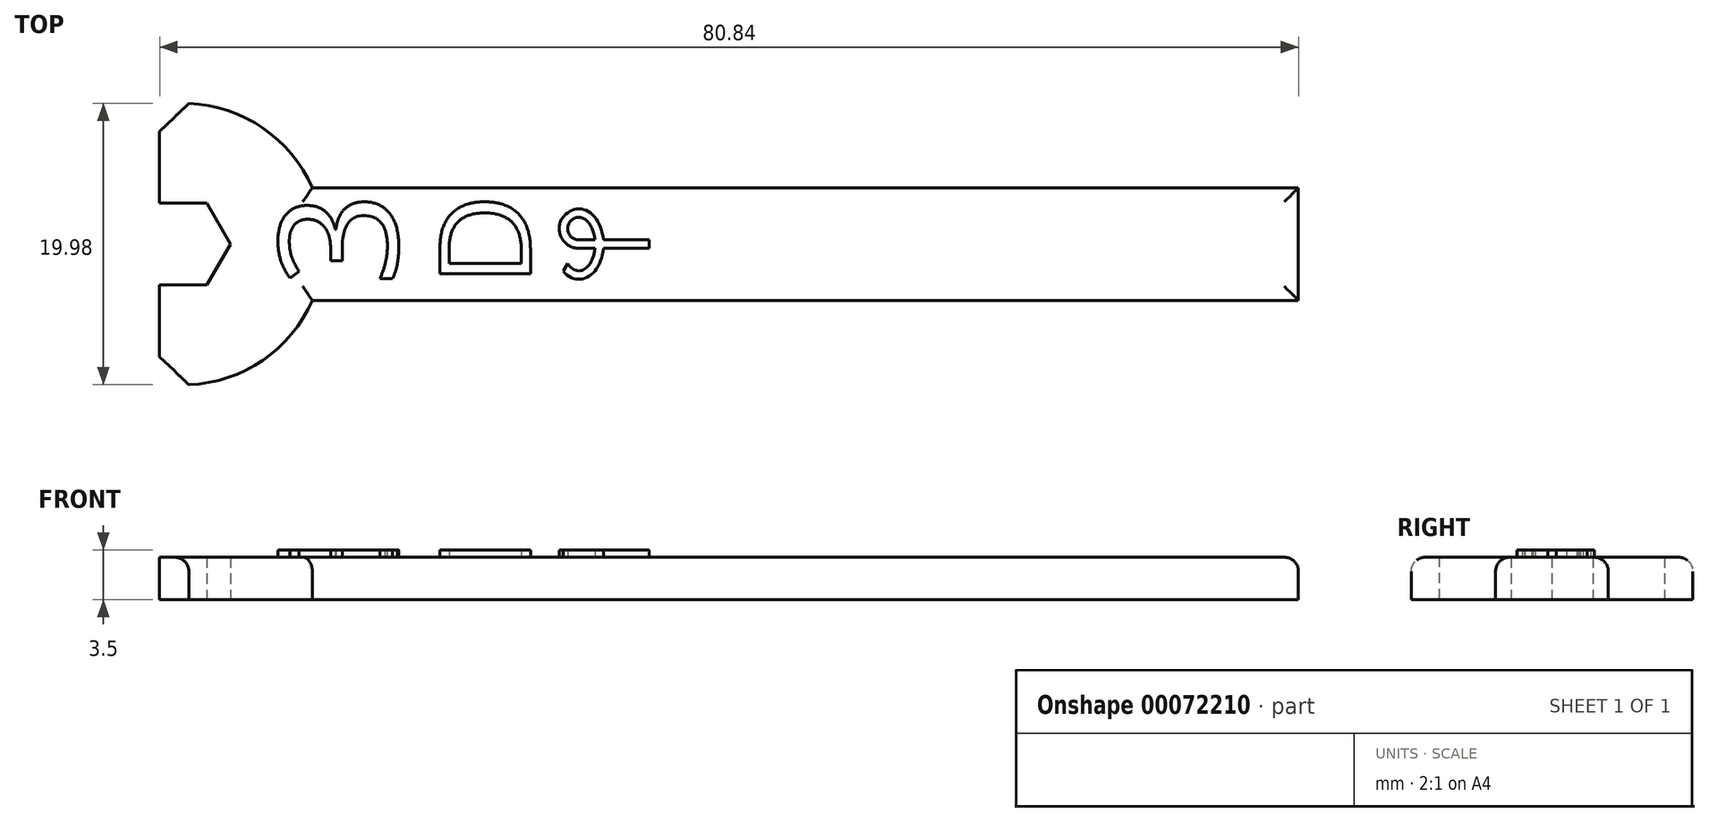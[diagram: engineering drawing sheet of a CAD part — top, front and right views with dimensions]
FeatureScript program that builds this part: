
annotation { "Feature Type Name" : "Feature", "Feature Type Description" : "" }
export const myFeature = defineFeature(function(context is Context, id is Id, definition is map)
    precondition{}
    {
        {
            var Q0;
            Q0=qCreatedBy(makeId("Top.planeOp"),FACE);
            var sketch = newSketch(context, id + "F0", { "sketchPlane" : qUnion([Q0])});
            skCircle(sketch, "E0.cCircle", {"center": v(0, 0) * mm, "radius": 2.9 * mm, "construction": true});
            skLineSegment(sketch, "E0.0", {"start": v(-3.35, 0) * mm, "end": v(-1.67, 2.9) * mm, "construction": true});
            skLineSegment(sketch, "E0.1", {"start": v(-1.67, 2.9) * mm, "end": v(1.67, 2.9) * mm});
            skLineSegment(sketch, "E0.2", {"start": v(1.67, 2.9) * mm, "end": v(3.35, 0) * mm});
            skLineSegment(sketch, "E0.3", {"start": v(3.35, 0) * mm, "end": v(1.67, -2.9) * mm});
            skLineSegment(sketch, "E0.4", {"start": v(1.67, -2.9) * mm, "end": v(-1.67, -2.9) * mm});
            skLineSegment(sketch, "E0.5", {"start": v(-1.67, -2.9) * mm, "end": v(-3.35, 0) * mm, "construction": true});
            skArc(sketch, "E1", {"start": v(9.17, 4) * mm, "mid": v(4.75, 8.8) * mm, "end": v(-1.67, 9.86) * mm});
            skLineSegment(sketch, "E2.bottom", {"start": v(9.17, 4) * mm, "end": v(79.17, 4) * mm});
            skLineSegment(sketch, "E2.top", {"start": v(9.17, -4) * mm, "end": v(79.17, -4) * mm});
            skLineSegment(sketch, "E2.right", {"start": v(79.17, 4) * mm, "end": v(79.17, -4) * mm});
            skArc(sketch, "E3.trimOffspring", {"start": v(-1.67, -9.86) * mm, "mid": v(4.75, -8.8) * mm, "end": v(9.17, -4) * mm});
            skLineSegment(sketch, "E4", {"start": v(-1.67, -9.86) * mm, "end": v(-1.67, -2.9) * mm});
            skLineSegment(sketch, "E5", {"start": v(-1.67, 2.9) * mm, "end": v(-1.67, 9.86) * mm});
            skSolve(sketch);
        }
        {
            var Q0;
            Q0=qSketchRegion(id+"F0",true);
            extrude(context, id + "F1", {"entities" : qUnion([Q0]), "depth" : 3 * mm});
        }
        {
            var Q0;
            Q0=makeQuery(id+"F1.opExtrude","SWEPT_EDGE",EDGE,{"disambiguationData":[OSD([sQuery(id+"F0.wireOp",EDGE,"E3.trimOffspring"),sQuery(id+"F0.wireOp",EDGE,"E4")])]});
            var Q1;
            Q1=makeQuery(id+"F1.opExtrude","SWEPT_EDGE",EDGE,{"disambiguationData":[OSD([sQuery(id+"F0.wireOp",EDGE,"E1"),sQuery(id+"F0.wireOp",EDGE,"E5")])]});
            chamfer(context, id + "F2", {"entities" : qUnion([Q0, Q1]), "width" : 2 * mm, "tangentPropagation" : true});
        }
        {
            var Q0;
            Q0=makeQuery(id+"F1.opExtrude","CAP_EDGE",EDGE,{"disambiguationData":[OSD([sQuery(id+"F0.wireOp",EDGE,"E1")])],"isStart":false});
            var Q1;
            Q1=makeQuery(id+"F1.opExtrude","CAP_EDGE",EDGE,{"disambiguationData":[OSD([sQuery(id+"F0.wireOp",EDGE,"E2.top")])],"isStart":false});
            var Q2;
            Q2=makeQuery(id+"F1.opExtrude","CAP_EDGE",EDGE,{"disambiguationData":[OSD([sQuery(id+"F0.wireOp",EDGE,"E2.bottom")])],"isStart":false});
            var Q3;
            Q3=makeQuery(id+"F1.opExtrude","CAP_EDGE",EDGE,{"disambiguationData":[OSD([sQuery(id+"F0.wireOp",EDGE,"E2.right")])],"isStart":false});
            var Q4;
            Q4=makeQuery(id+"F1.opExtrude","CAP_EDGE",EDGE,{"disambiguationData":[OSD([sQuery(id+"F0.wireOp",EDGE,"E3.trimOffspring")])],"isStart":false});
            fillet(context, id + "F3", {"entities" : qUnion([Q0, Q1, Q2, Q3, Q4]), "radius" : 1 * mm, "tangentPropagation" : true, "allowEdgeOverflow" : false});
        }
        {
            var Q0;
            Q0=makeQuery(id+"F1.opExtrude","CAP_FACE",FACE,{"disambiguationData":[OSD([sQuery(id+"F0.wireOp",EDGE,"E0.0"),sQuery(id+"F0.wireOp",EDGE,"E0.1"),sQuery(id+"F0.wireOp",EDGE,"E0.2"),sQuery(id+"F0.wireOp",EDGE,"E0.3"),sQuery(id+"F0.wireOp",EDGE,"E0.4"),sQuery(id+"F0.wireOp",EDGE,"E0.5"),sQuery(id+"F0.wireOp",EDGE,"E1"),sQuery(id+"F0.wireOp",EDGE,"E2.bottom"),sQuery(id+"F0.wireOp",EDGE,"E2.top"),sQuery(id+"F0.wireOp",EDGE,"E2.right")])],"isStart":false});
            var sketch = newSketch(context, id + "F4", { "sketchPlane" : qUnion([Q0])});
            skText(sketch, "E6", { "text": "3\n", "fontName": "OpenSans-Regular.ttf"});
            skText(sketch, "E7", { "text": "D", "fontName": "OpenSans-Regular.ttf"});
            const initialGuessF4  = {"E6": [0.01519, -0.003, 0, 1, 0.00842], "E7": [0.02465, -0.003, 0, 1, 0.00647]};
            skSetInitialGuess(sketch, initialGuessF4);
            skSolve(sketch);
        }
        {
            var Q0;
            Q0=qSketchRegion(id+"F4",true);
            extrude(context, id + "F5", {"entities" : qUnion([Q0]), "operationType" : NewBodyOperationType.ADD, "depth" : 0.5 * mm});
        }
        {
            var Q0;
            Q0=makeQuery(id+"F4.imprint","IMPRINT",FACE,{"disambiguationData":[TD([[makeQuery(id+"F4.imprint","IMPRINT",EDGE,{"derivedFrom":sQuery(id+"F4.wireOp",EDGE,"E6.sketch_text.stroke-0")}),1.0]])]});
            var sketch = newSketch(context, id + "F6", { "sketchPlane" : qUnion([Q0])});
            skLineSegment(sketch, "E8.rect.bottom", {"start": v(28.09, 0.3) * mm, "end": v(33.09, 0.3) * mm});
            skLineSegment(sketch, "E8.rect.top", {"start": v(28.09, -0.3) * mm, "end": v(33.09, -0.3) * mm});
            skLineSegment(sketch, "E8.rect.left", {"start": v(28.09, 0.3) * mm, "end": v(28.09, -0.3) * mm});
            skLineSegment(sketch, "E8.rect.right", {"start": v(33.09, 0.3) * mm, "end": v(33.09, -0.3) * mm});
            skPoint(sketch, "E8.rect.middle", {"position": v(30.59, 0) * mm});
            skLineSegment(sketch, "E9", {"start": v(28.09, 0.3) * mm, "end": v(28.09, 4.53) * mm, "construction": true});
            skArc(sketch, "E10", {"start": v(28.09, 1.9) * mm, "mid": v(27.29, 1.1) * mm, "end": v(28.09, 0.3) * mm});
            skArc(sketch, "E11", {"start": v(28.09, 2.5) * mm, "mid": v(26.69, 1.1) * mm, "end": v(28.09, -0.3) * mm});
            skPoint(sketch, "E12", {"position": v(28.09, 0) * mm});
            skEllipse(sketch, "E13", {"center": v(28.09, 0) * mm, "majorRadius": 2.5 * mm, "minorRadius": 1.75 * mm, "majorAxis": v(0, 1)});
            skEllipse(sketch, "E14", {"center": v(28.09, 0) * mm, "majorRadius": 1.9 * mm, "minorRadius": 1.15 * mm, "majorAxis": v(0, 1)});
            skLineSegment(sketch, "E15", {"start": v(28.09, 0) * mm, "end": v(26.98, -1.93) * mm});
            skPoint(sketch, "E16", {"position": v(27.3, -1.37) * mm});
            skPoint(sketch, "E17", {"position": v(26.98, -1.93) * mm});
            skSolve(sketch);
        }
        {
            var Q0;
            {var subQ0=sQuery(id+"F6.wireOp",EDGE,"E8.rect.right");Q0=makeQuery(id+"F6.imprint","IMPRINT",FACE,{"disambiguationData":[TD([[makeQuery(id+"F6.imprint","IMPRINT",EDGE,{"derivedFrom":subQ0}),-1.0]])]});}
            var Q1;
            {var subQ0=sQuery(id+"F6.wireOp",EDGE,"E14");var subQ1=sQuery(id+"F6.wireOp",EDGE,"E8.rect.bottom");var subQ2=makeQuery(id+"F6.imprint","INTERSECT",VERTEX,{"derivedFrom":[subQ1,subQ0]});Q1=makeQuery(id+"F6.imprint","IMPRINT",FACE,{"disambiguationData":[TD([[makeQuery(id+"F6.imprint","IMPRINT",EDGE,{"disambiguationData":[TD([[subQ2,-1.0]])],"derivedFrom":subQ1}),-1.0]])]});}
            var Q2;
            {var subQ4=sQuery(id+"F6.wireOp",EDGE,"E14");var subQ6=sQuery(id+"F6.wireOp",EDGE,"E8.rect.bottom");var subQ8=makeQuery(id+"F6.imprint","INTERSECT",VERTEX,{"derivedFrom":[subQ6,subQ4]});Q2=makeQuery(id+"F6.imprint","IMPRINT",FACE,{"disambiguationData":[TD([[makeQuery(id+"F6.imprint","IMPRINT",EDGE,{"disambiguationData":[TD([[subQ8,1.0]])],"derivedFrom":subQ4}),1.0]])]});}
            var Q3;
            {var subQ1=sQuery(id+"F6.wireOp",EDGE,"E8.rect.left");var subQ3=sQuery(id+"F6.wireOp",EDGE,"E15");var subQ4=makeQuery(id+"F6.imprint","INTERSECT",VERTEX,{"derivedFrom":[subQ1,subQ3]});Q3=makeQuery(id+"F6.imprint","IMPRINT",FACE,{"disambiguationData":[TD([[makeQuery(id+"F6.imprint","IMPRINT",EDGE,{"disambiguationData":[TD([[subQ4,-1.0]])],"derivedFrom":subQ3}),1.0]])]});}
            var Q4;
            {var subQ1=sQuery(id+"F6.wireOp",EDGE,"E10");Q4=makeQuery(id+"F6.imprint","IMPRINT",FACE,{"disambiguationData":[TD([[makeQuery(id+"F6.imprint","IMPRINT",EDGE,{"derivedFrom":subQ1}),-1.0]])]});}
            var Q5;
            {var subQ0=sQuery(id+"F6.wireOp",EDGE,"E14");var subQ6=sQuery(id+"F6.wireOp",EDGE,"E8.rect.bottom");var subQ8=makeQuery(id+"F6.imprint","INTERSECT",VERTEX,{"derivedFrom":[subQ6,subQ0]});Q5=makeQuery(id+"F6.imprint","IMPRINT",FACE,{"disambiguationData":[TD([[makeQuery(id+"F6.imprint","IMPRINT",EDGE,{"disambiguationData":[TD([[subQ8,-1.0]])],"derivedFrom":subQ6}),1.0]])]});}
            var Q6;
            {var subQ0=sQuery(id+"F6.wireOp",EDGE,"E14");var subQ1=sQuery(id+"F6.wireOp",EDGE,"E8.rect.top");var subQ2=makeQuery(id+"F6.imprint","INTERSECT",VERTEX,{"derivedFrom":[subQ1,subQ0]});Q6=makeQuery(id+"F6.imprint","IMPRINT",FACE,{"disambiguationData":[TD([[makeQuery(id+"F6.imprint","IMPRINT",EDGE,{"disambiguationData":[TD([[subQ2,-1.0]])],"derivedFrom":subQ1}),-1.0]])]});}
            extrude(context, id + "F7", {"entities" : qUnion([Q0, Q1, Q2, Q3, Q4, Q5, Q6]), "operationType" : NewBodyOperationType.ADD, "depth" : 0.5 * mm});
        }
    });
